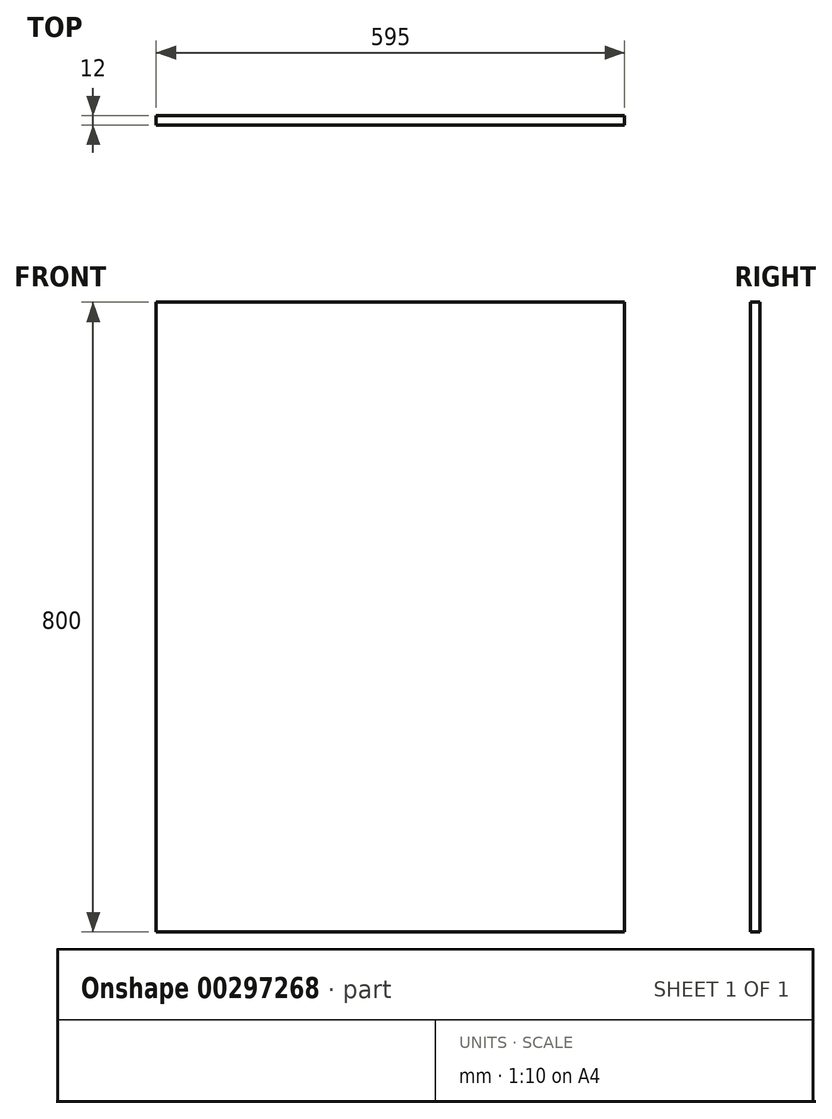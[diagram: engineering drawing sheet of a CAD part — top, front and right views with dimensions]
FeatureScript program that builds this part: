
annotation { "Feature Type Name" : "Feature", "Feature Type Description" : "" }
export const myFeature = defineFeature(function(context is Context, id is Id, definition is map)
    precondition{}
    {
        {
            var Q0;
            Q0=qCreatedBy(makeId("Front.planeOp"),FACE);
            var sketch = newSketch(context, id + "F0", { "sketchPlane" : qUnion([Q0])});
            skLineSegment(sketch, "E0.bottom", {"start": v(297.5, 400) * mm, "end": v(-297.5, 400) * mm});
            skLineSegment(sketch, "E0.top", {"start": v(297.5, -400) * mm, "end": v(-297.5, -400) * mm});
            skLineSegment(sketch, "E0.left", {"start": v(297.5, 400) * mm, "end": v(297.5, -400) * mm});
            skLineSegment(sketch, "E0.right", {"start": v(-297.5, 400) * mm, "end": v(-297.5, -400) * mm});
            skPoint(sketch, "E0.middle", {"position": v(0, 0) * mm});
            skSolve(sketch);
        }
        {
            var Q0;
            Q0 = qSketchRegion(id + "F0", true);
            extrude(context, id + "F1", {"entities" : qUnion([Q0]), "depth" : 12 * mm});
        }
    });
